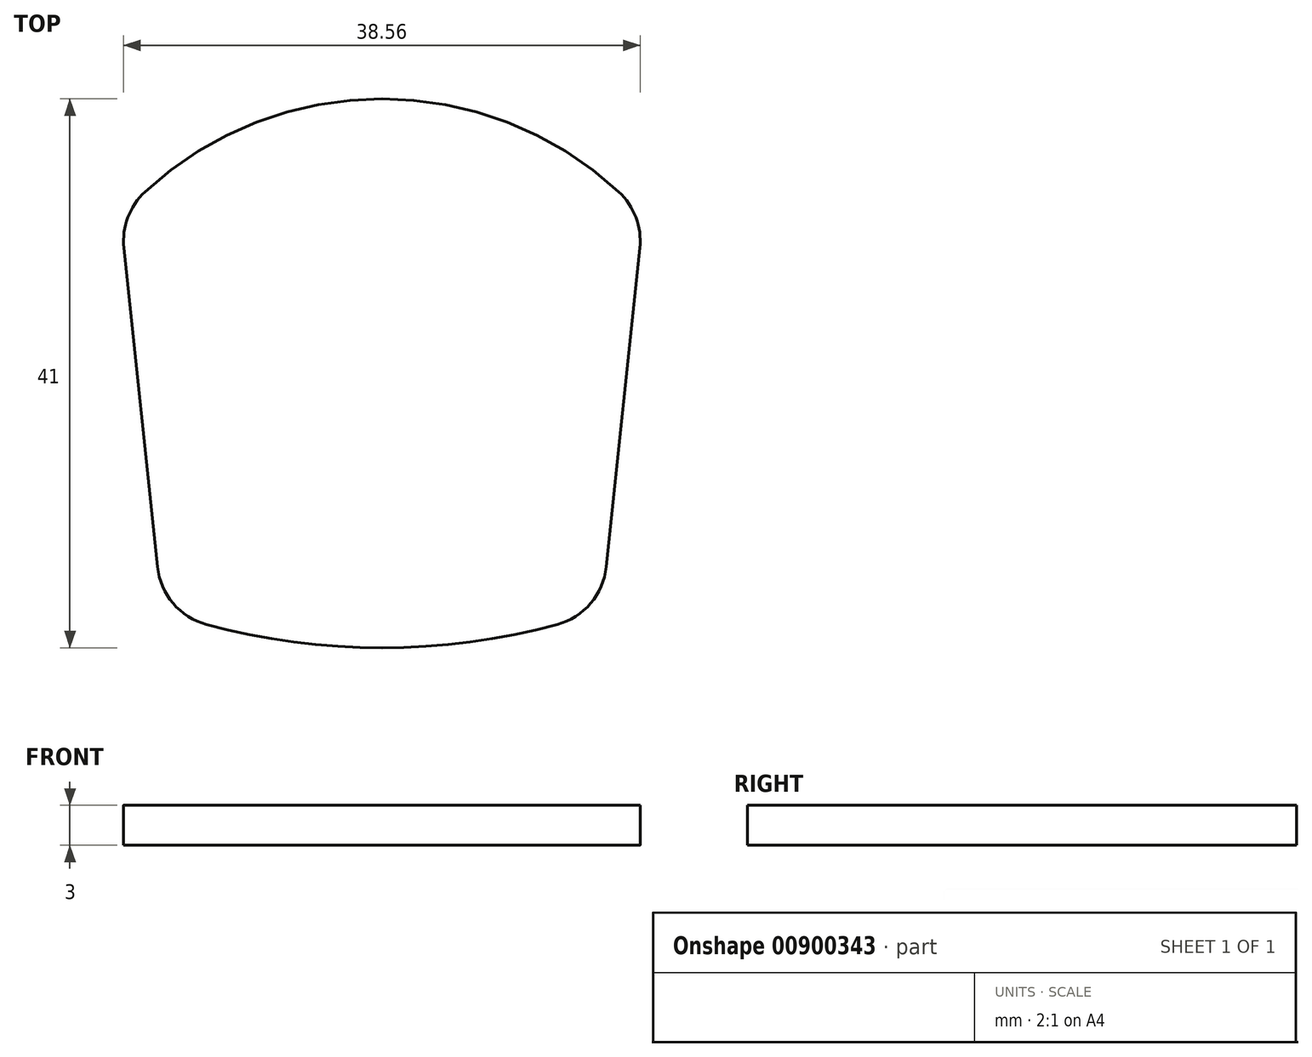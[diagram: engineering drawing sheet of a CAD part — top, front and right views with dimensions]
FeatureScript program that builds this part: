
annotation { "Feature Type Name" : "Feature", "Feature Type Description" : "" }
export const myFeature = defineFeature(function(context is Context, id is Id, definition is map)
    precondition{}
    {
        {
            var Q0;
            Q0=qCreatedBy(makeId("Top.planeOp"),FACE);
            var sketch = newSketch(context, id + "F0", { "sketchPlane" : qUnion([Q0])});
            skLineSegment(sketch, "E0", {"start": v(-16.75, 3.28) * mm, "end": v(-19.26, 27.1) * mm});
            skLineSegment(sketch, "E1", {"start": v(16.75, 3.28) * mm, "end": v(19.26, 27.1) * mm});
            skArc(sketch, "E2", {"start": v(17.68, 31.3) * mm, "mid": v(0, 38.23) * mm, "end": v(-17.68, 31.3) * mm});
            skArc(sketch, "E3", {"start": v(-13.09, -1.03) * mm, "mid": v(0, -2.77) * mm, "end": v(13.09, -1.03) * mm});
            skLineSegment(sketch, "E4.bottom", {"start": v(29.93, 47.43) * mm, "end": v(-29.93, 47.43) * mm, "construction": true});
            skLineSegment(sketch, "E4.top", {"start": v(29.93, -12.43) * mm, "end": v(-29.93, -12.43) * mm, "construction": true});
            skLineSegment(sketch, "E4.left", {"start": v(29.93, 47.43) * mm, "end": v(29.93, -12.43) * mm, "construction": true});
            skLineSegment(sketch, "E4.right", {"start": v(-29.93, 47.43) * mm, "end": v(-29.93, -12.43) * mm, "construction": true});
            skPoint(sketch, "E4.middle", {"position": v(0, 17.5) * mm});
            skPoint(sketch, "E5.visualSharp", {"position": v(-19.5, 29.43) * mm});
            skArc(sketch, "E5.filletArc", {"start": v(-17.68, 31.3) * mm, "mid": v(-18.96, 29.38) * mm, "end": v(-19.26, 27.1) * mm});
            skPoint(sketch, "E6.visualSharp", {"position": v(19.5, 29.43) * mm});
            skArc(sketch, "E6.filletArc", {"start": v(19.26, 27.1) * mm, "mid": v(18.96, 29.38) * mm, "end": v(17.68, 31.3) * mm});
            skPoint(sketch, "E7.visualSharp", {"position": v(16.4, 0) * mm});
            skArc(sketch, "E7.filletArc", {"start": v(13.09, -1.03) * mm, "mid": v(15.59, 0.56) * mm, "end": v(16.75, 3.28) * mm});
            skPoint(sketch, "E8.visualSharp", {"position": v(-16.4, 0) * mm});
            skArc(sketch, "E8.filletArc", {"start": v(-16.75, 3.28) * mm, "mid": v(-15.59, 0.56) * mm, "end": v(-13.09, -1.03) * mm});
            skCircle(sketch, "E9", {"center": v(-30, -27.5) * mm, "radius": 10 * mm, "construction": true});
            skCircle(sketch, "E10", {"center": v(-14.28, 27.63) * mm, "radius": 5 * mm, "construction": true});
            skCircle(sketch, "E11", {"center": v(14.28, 27.63) * mm, "radius": 5 * mm, "construction": true});
            skCircle(sketch, "E12", {"center": v(11.78, 3.8) * mm, "radius": 5 * mm, "construction": true});
            skCircle(sketch, "E13", {"center": v(-11.78, 3.8) * mm, "radius": 5 * mm, "construction": true});
            skCircle(sketch, "E14", {"center": v(-45, 42.5) * mm, "radius": 10 * mm, "construction": true});
            skCircle(sketch, "E15", {"center": v(-38.3, -12.5) * mm, "radius": 3 * mm});
            skSolve(sketch);
        }
        {
            var Q0;
            Q0=makeQuery(id+"F0.imprint","IMPRINT",FACE,{"disambiguationData":[TD([[makeQuery(id+"F0.imprint","IMPRINT",EDGE,{"derivedFrom":sQuery(id+"F0.wireOp",EDGE,"E0")}),-1.0]])]});
            extrude(context, id + "F1", {"entities" : qUnion([Q0]), "depth" : 3 * mm, "offsetDistance" : 25 * mm});
        }
    });
